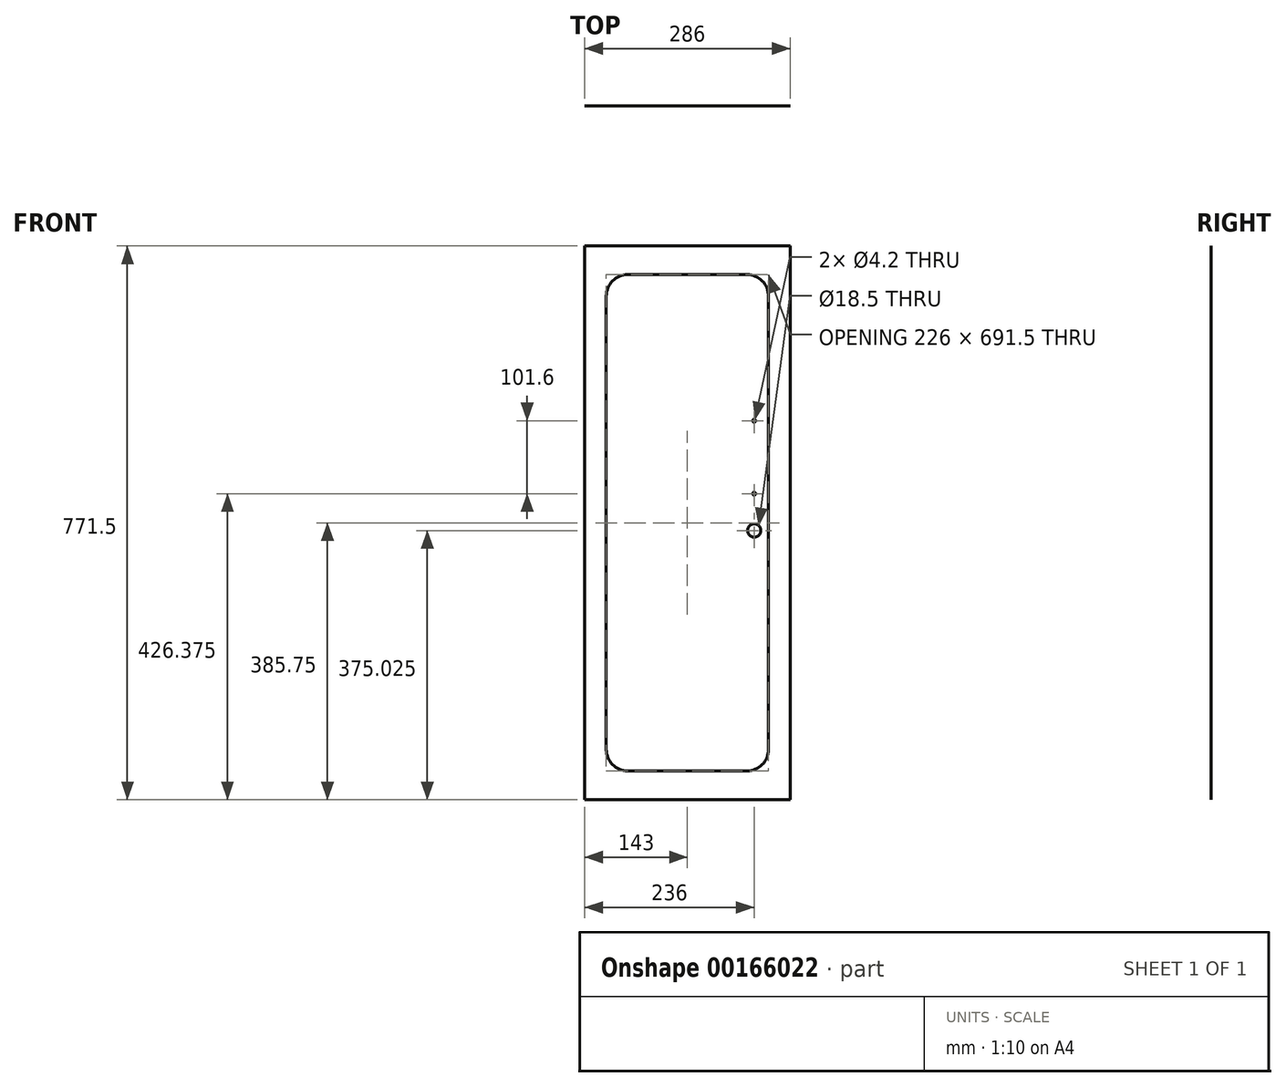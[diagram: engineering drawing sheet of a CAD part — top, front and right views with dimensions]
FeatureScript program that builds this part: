
annotation { "Feature Type Name" : "Feature", "Feature Type Description" : "" }
export const myFeature = defineFeature(function(context is Context, id is Id, definition is map)
    precondition{}
    {
        {
            var Q0;
            Q0=qCreatedBy(makeId("Front.planeOp"),FACE);
            var sketch = newSketch(context, id + "F0", { "sketchPlane" : qUnion([Q0])});
            skLineSegment(sketch, "E0.bottom", {"start": v(0, 0) * mm, "end": v(286, 0) * mm});
            skLineSegment(sketch, "E0.top", {"start": v(0, 771.5) * mm, "end": v(286, 771.5) * mm});
            skLineSegment(sketch, "E0.left", {"start": v(0, 0) * mm, "end": v(0, 771.5) * mm});
            skLineSegment(sketch, "E0.right", {"start": v(286, 0) * mm, "end": v(286, 771.5) * mm});
            skLineSegment(sketch, "E1", {"start": v(10, 771.5) * mm, "end": v(10, 0) * mm, "construction": true});
            skLineSegment(sketch, "E2", {"start": v(0, 731.5) * mm, "end": v(286, 731.5) * mm, "construction": true});
            skLineSegment(sketch, "E3", {"start": v(276, 771.5) * mm, "end": v(276, 0) * mm, "construction": true});
            skLineSegment(sketch, "E4", {"start": v(286, 40) * mm, "end": v(0, 40) * mm, "construction": true});
            skLineSegment(sketch, "E5.bottom", {"start": v(60, 731.5) * mm, "end": v(226, 731.5) * mm});
            skLineSegment(sketch, "E5.top", {"start": v(60, 40) * mm, "end": v(226, 40) * mm});
            skLineSegment(sketch, "E5.left", {"start": v(30, 701.5) * mm, "end": v(30, 70) * mm});
            skLineSegment(sketch, "E5.right", {"start": v(256, 701.5) * mm, "end": v(256, 70) * mm});
            skPoint(sketch, "E6.visualSharp", {"position": v(30, 731.5) * mm});
            skArc(sketch, "E6.filletArc", {"start": v(60, 731.5) * mm, "mid": v(38.79, 722.71) * mm, "end": v(30, 701.5) * mm});
            skPoint(sketch, "E7.visualSharp", {"position": v(256, 731.5) * mm});
            skArc(sketch, "E7.filletArc", {"start": v(256, 701.5) * mm, "mid": v(247.21, 722.71) * mm, "end": v(226, 731.5) * mm});
            skPoint(sketch, "E8.visualSharp", {"position": v(30, 40) * mm});
            skArc(sketch, "E8.filletArc", {"start": v(30, 70) * mm, "mid": v(38.79, 48.79) * mm, "end": v(60, 40) * mm});
            skPoint(sketch, "E9.visualSharp", {"position": v(256, 40) * mm});
            skArc(sketch, "E9.filletArc", {"start": v(226, 40) * mm, "mid": v(247.21, 48.79) * mm, "end": v(256, 70) * mm});
            skLineSegment(sketch, "E10", {"start": v(236, 527.98) * mm, "end": v(236, 426.38) * mm, "construction": true});
            skCircle(sketch, "E11", {"center": v(236, 527.98) * mm, "radius": 2.1 * mm});
            skCircle(sketch, "E12", {"center": v(236, 426.38) * mm, "radius": 2.1 * mm});
            skLineSegment(sketch, "E13", {"start": v(30, 385.75) * mm, "end": v(10, 385.75) * mm, "construction": true});
            skLineSegment(sketch, "E14", {"start": v(256, 385.75) * mm, "end": v(276, 385.75) * mm, "construction": true});
            skLineSegment(sketch, "E15", {"start": v(236, 426.38) * mm, "end": v(236, 375.03) * mm, "construction": true});
            skCircle(sketch, "E16", {"center": v(236, 375.03) * mm, "radius": 9.25 * mm});
            skPoint(sketch, "E17", {"position": v(236, 451.5) * mm});
            skLineSegment(sketch, "E18", {"start": v(30, 451.5) * mm, "end": v(256, 451.5) * mm, "construction": true});
            skSolve(sketch);
        }
        {
            var Q0;
            Q0=makeQuery(id+"F0.imprint","IMPRINT",FACE,{"disambiguationData":[TD([[makeQuery(id+"F0.imprint","IMPRINT",EDGE,{"derivedFrom":sQuery(id+"F0.wireOp",EDGE,"E0.bottom")}),1.0]])]});
            extrude(context, id + "F1", {"entities" : qUnion([Q0]), "depth" : 1 / 203.2 * mm});
        }
        {
            var Q0;
            Q0=makeQuery(id+"F0.imprint","IMPRINT",FACE,{"disambiguationData":[TD([[makeQuery(id+"F0.imprint","IMPRINT",EDGE,{"derivedFrom":sQuery(id+"F0.wireOp",EDGE,"E5.bottom")}),-1.0]])]});
            extrude(context, id + "F2", {"entities" : qUnion([Q0]), "depth" : 1 / 203.2 * mm});
        }
    });
